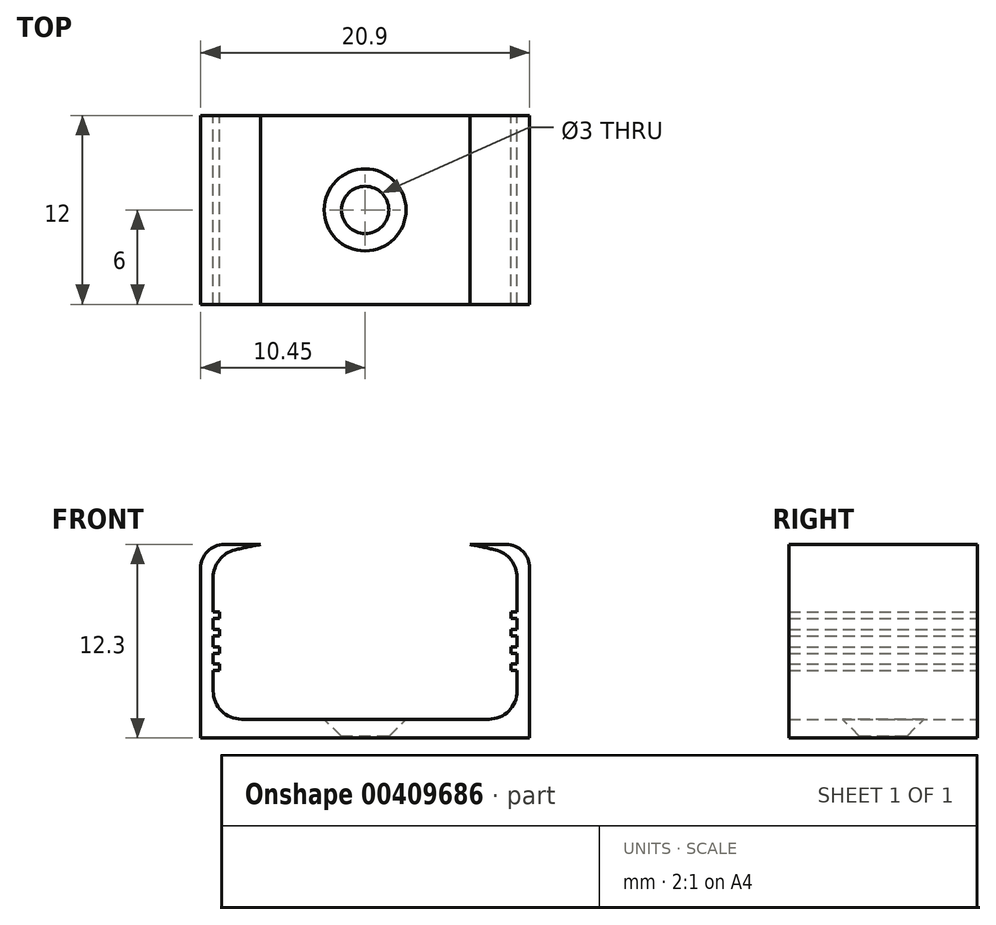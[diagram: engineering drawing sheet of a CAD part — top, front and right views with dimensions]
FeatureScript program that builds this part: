
annotation { "Feature Type Name" : "Feature", "Feature Type Description" : "" }
export const myFeature = defineFeature(function(context is Context, id is Id, definition is map)
    precondition{}
    {
        {
            var Q0;
            Q0=qCreatedBy(makeId("Front.planeOp"),FACE);
            var sketch = newSketch(context, id + "F0", { "sketchPlane" : qUnion([Q0])});
            skLineSegment(sketch, "E0.top", {"start": v(-7.85, -5.2) * mm, "end": v(7.85, -5.2) * mm});
            skLineSegment(sketch, "E0.left", {"start": v(-9.65, 3.8) * mm, "end": v(-9.65, -3.4) * mm});
            skLineSegment(sketch, "E0.right", {"start": v(9.65, 3.8) * mm, "end": v(9.65, -3.4) * mm});
            skPoint(sketch, "E0.middle", {"position": v(0, 0) * mm});
            skArc(sketch, "E1", {"start": v(-8.26, 5.56) * mm, "mid": v(0, 6.52) * mm, "end": v(8.26, 5.56) * mm, "construction": true});
            skPoint(sketch, "E2", {"position": v(-1.1, 6.5) * mm});
            skPoint(sketch, "E3", {"position": v(0, -5.2) * mm});
            skPoint(sketch, "E4.visualSharp", {"position": v(-9.65, 5.2) * mm});
            skArc(sketch, "E4.filletArc", {"start": v(-8.26, 5.56) * mm, "mid": v(-9.26, 4.92) * mm, "end": v(-9.65, 3.8) * mm});
            skPoint(sketch, "E5.visualSharp", {"position": v(9.65, 5.2) * mm});
            skArc(sketch, "E5.filletArc", {"start": v(9.65, 3.8) * mm, "mid": v(9.26, 4.92) * mm, "end": v(8.26, 5.56) * mm});
            skPoint(sketch, "E6.visualSharp", {"position": v(-9.65, -5.2) * mm});
            skArc(sketch, "E6.filletArc", {"start": v(-9.65, -3.4) * mm, "mid": v(-9.12, -4.67) * mm, "end": v(-7.85, -5.2) * mm});
            skPoint(sketch, "E7.visualSharp", {"position": v(9.65, -5.2) * mm});
            skArc(sketch, "E7.filletArc", {"start": v(7.85, -5.2) * mm, "mid": v(9.12, -4.67) * mm, "end": v(9.65, -3.4) * mm});
            skLineSegment(sketch, "E8", {"start": v(-6.65, 8.98) * mm, "end": v(-6.65, -16.18) * mm, "construction": true});
            skLineSegment(sketch, "E9", {"start": v(6.65, 11.26) * mm, "end": v(6.65, -16.47) * mm, "construction": true});
            skLineSegment(sketch, "E10.top", {"start": v(-10.45, -6.4) * mm, "end": v(10.45, -6.4) * mm});
            skPoint(sketch, "E11", {"position": v(-6.65, 5.9) * mm});
            skPoint(sketch, "E12", {"position": v(6.65, 5.9) * mm});
            skLineSegment(sketch, "E13", {"start": v(-6.65, 5.9) * mm, "end": v(-8.95, 5.9) * mm});
            skLineSegment(sketch, "E14", {"start": v(6.65, 5.9) * mm, "end": v(8.95, 5.9) * mm});
            skLineSegment(sketch, "E15", {"start": v(10.45, 4.4) * mm, "end": v(10.45, -6.4) * mm});
            skLineSegment(sketch, "E16", {"start": v(-10.45, -6.4) * mm, "end": v(-10.45, 4.4) * mm});
            skArc(sketch, "E17", {"start": v(-8.26, 5.56) * mm, "mid": v(-7.46, 5.74) * mm, "end": v(-6.65, 5.9) * mm});
            skArc(sketch, "E18", {"start": v(8.26, 5.56) * mm, "mid": v(7.46, 5.74) * mm, "end": v(6.65, 5.9) * mm});
            skPoint(sketch, "E19.visualSharp", {"position": v(-10.45, 5.9) * mm});
            skArc(sketch, "E19.filletArc", {"start": v(-8.95, 5.9) * mm, "mid": v(-10.01, 5.46) * mm, "end": v(-10.45, 4.4) * mm});
            skPoint(sketch, "E20.visualSharp", {"position": v(10.45, 5.9) * mm});
            skArc(sketch, "E20.filletArc", {"start": v(10.45, 4.4) * mm, "mid": v(10.01, 5.46) * mm, "end": v(8.95, 5.9) * mm});
            skLineSegment(sketch, "E21", {"start": v(-18.56, 1.4) * mm, "end": v(25.3, 1.4) * mm, "construction": true});
            skLineSegment(sketch, "E22", {"start": v(-18.95, 0.3) * mm, "end": v(25.3, 0.3) * mm, "construction": true});
            skLineSegment(sketch, "E23", {"start": v(-19.22, -0.8) * mm, "end": v(25.82, -0.8) * mm, "construction": true});
            skLineSegment(sketch, "E24", {"start": v(-19.08, -1.9) * mm, "end": v(26.08, -1.9) * mm, "construction": true});
            skLineSegment(sketch, "E25.bottom", {"start": v(-9.25, -1.7) * mm, "end": v(-10.05, -1.7) * mm});
            skLineSegment(sketch, "E25.top", {"start": v(-9.25, -2.1) * mm, "end": v(-10.05, -2.1) * mm});
            skLineSegment(sketch, "E25.left", {"start": v(-9.25, -1.7) * mm, "end": v(-9.25, -2.1) * mm});
            skLineSegment(sketch, "E25.right", {"start": v(-10.05, -1.7) * mm, "end": v(-10.05, -2.1) * mm});
            skPoint(sketch, "E25.middle", {"position": v(-9.65, -1.9) * mm});
            skLineSegment(sketch, "E26.bottom", {"start": v(-9.25, -1) * mm, "end": v(-10.05, -1) * mm});
            skLineSegment(sketch, "E26.top", {"start": v(-9.25, -0.6) * mm, "end": v(-10.05, -0.6) * mm});
            skLineSegment(sketch, "E26.left", {"start": v(-9.25, -1) * mm, "end": v(-9.25, -0.6) * mm});
            skLineSegment(sketch, "E26.right", {"start": v(-10.05, -1) * mm, "end": v(-10.05, -0.6) * mm});
            skPoint(sketch, "E26.middle", {"position": v(-9.65, -0.8) * mm});
            skLineSegment(sketch, "E27.bottom", {"start": v(-9.25, 0.1) * mm, "end": v(-10.05, 0.1) * mm});
            skLineSegment(sketch, "E27.top", {"start": v(-9.25, 0.5) * mm, "end": v(-10.05, 0.5) * mm});
            skLineSegment(sketch, "E27.left", {"start": v(-9.25, 0.1) * mm, "end": v(-9.25, 0.5) * mm});
            skLineSegment(sketch, "E27.right", {"start": v(-10.05, 0.1) * mm, "end": v(-10.05, 0.5) * mm});
            skPoint(sketch, "E27.middle", {"position": v(-9.65, 0.3) * mm});
            skLineSegment(sketch, "E28.bottom", {"start": v(-9.25, 1.2) * mm, "end": v(-10.05, 1.2) * mm});
            skLineSegment(sketch, "E28.top", {"start": v(-9.25, 1.6) * mm, "end": v(-10.05, 1.6) * mm});
            skLineSegment(sketch, "E28.left", {"start": v(-9.25, 1.2) * mm, "end": v(-9.25, 1.6) * mm});
            skLineSegment(sketch, "E28.right", {"start": v(-10.05, 1.2) * mm, "end": v(-10.05, 1.6) * mm});
            skPoint(sketch, "E28.middle", {"position": v(-9.65, 1.4) * mm});
            skLineSegment(sketch, "E29.MirrorCS", {"start": v(9.25, 1.2) * mm, "end": v(9.25, 1.6) * mm});
            skLineSegment(sketch, "E30.MirrorCS", {"start": v(9.25, 1.6) * mm, "end": v(10.05, 1.6) * mm});
            skLineSegment(sketch, "E31.MirrorCS", {"start": v(9.25, 1.2) * mm, "end": v(10.05, 1.2) * mm});
            skLineSegment(sketch, "E32.MirrorCS", {"start": v(10.05, 1.2) * mm, "end": v(10.05, 1.6) * mm});
            skLineSegment(sketch, "E33.MirrorCS", {"start": v(10.05, 0.1) * mm, "end": v(10.05, 0.5) * mm});
            skLineSegment(sketch, "E34.MirrorCS", {"start": v(9.25, 0.5) * mm, "end": v(10.05, 0.5) * mm});
            skLineSegment(sketch, "E35.MirrorCS", {"start": v(9.25, 0.1) * mm, "end": v(9.25, 0.5) * mm});
            skLineSegment(sketch, "E36.MirrorCS", {"start": v(9.25, 0.1) * mm, "end": v(10.05, 0.1) * mm});
            skLineSegment(sketch, "E37.MirrorCS", {"start": v(9.25, -0.6) * mm, "end": v(10.05, -0.6) * mm});
            skLineSegment(sketch, "E38.MirrorCS", {"start": v(9.25, -1) * mm, "end": v(9.25, -0.6) * mm});
            skLineSegment(sketch, "E39.MirrorCS", {"start": v(9.25, -1) * mm, "end": v(10.05, -1) * mm});
            skLineSegment(sketch, "E40.MirrorCS", {"start": v(10.05, -1) * mm, "end": v(10.05, -0.6) * mm});
            skLineSegment(sketch, "E41.MirrorCS", {"start": v(9.25, -1.7) * mm, "end": v(9.25, -2.1) * mm});
            skLineSegment(sketch, "E42.MirrorCS", {"start": v(9.25, -2.1) * mm, "end": v(10.05, -2.1) * mm});
            skLineSegment(sketch, "E43.MirrorCS", {"start": v(10.05, -1.7) * mm, "end": v(10.05, -2.1) * mm});
            skLineSegment(sketch, "E44.MirrorCS", {"start": v(9.25, -1.7) * mm, "end": v(10.05, -1.7) * mm});
            skLineSegment(sketch, "E45", {"start": v(-9.25, 2.38) * mm, "end": v(-9.25, -3.43) * mm, "construction": true});
            skSolve(sketch);
        }
        {
            var Q0;
            Q0 = qSketchRegion(id + "F0", true);
            extrude(context, id + "F1", {"entities" : qUnion([Q0]), "depth" : 6 * mm, "hasSecondDirection" : true, "secondDirectionOppositeDirection" : true, "secondDirectionDepth" : 6 * mm});
        }
        {
            var Q0;
            Q0=makeQuery(id+"F1.opExtrude","SWEPT_FACE",FACE,{"disambiguationData":[OSD([sQuery(id+"F0.wireOp",EDGE,"E0.top")])]});
            var sketch = newSketch(context, id + "F2", { "sketchPlane" : qUnion([Q0])});
            skPoint(sketch, "E46", {"position": v(0, 0) * mm});
            skSolve(sketch);
        }
        {
            var Q0;
            Q0=sQuery(id+"F2.wireOp",VERTEX,"E46");
            var Q1;
            Q1=makeQuery(id+"F1.opExtrude","SWEPT_BODY",BODY,{"disambiguationData":[OSD([sQuery(id+"F0.wireOp",EDGE,"E0.top"),sQuery(id+"F0.wireOp",EDGE,"E0.left"),sQuery(id+"F0.wireOp",EDGE,"E0.right"),sQuery(id+"F0.wireOp",EDGE,"E4.filletArc"),sQuery(id+"F0.wireOp",EDGE,"E5.filletArc"),sQuery(id+"F0.wireOp",EDGE,"E6.filletArc"),sQuery(id+"F0.wireOp",EDGE,"E7.filletArc"),sQuery(id+"F0.wireOp",EDGE,"E10.top"),sQuery(id+"F0.wireOp",EDGE,"E13"),sQuery(id+"F0.wireOp",EDGE,"E14"),sQuery(id+"F0.wireOp",EDGE,"E15"),sQuery(id+"F0.wireOp",EDGE,"E16"),sQuery(id+"F0.wireOp",EDGE,"E17"),sQuery(id+"F0.wireOp",EDGE,"E18"),sQuery(id+"F0.wireOp",EDGE,"E19.filletArc"),sQuery(id+"F0.wireOp",EDGE,"E20.filletArc")])]});
            hole(context, id + "F3", {"style" : HoleStyle.C_SINK, "endStyle" : HoleEndStyle.THROUGH, "holeDiameter" : 3 * mm, "cSinkDiameter" : 5.2 * mm, "cSinkAngle" : 90 * degree, "isTappedThrough" : true, "tappedDepth" : 12 * mm, "tapClearance" : 3, "locations" : qUnion([Q0]), "scope" : qUnion([Q1])});
        }
    });
